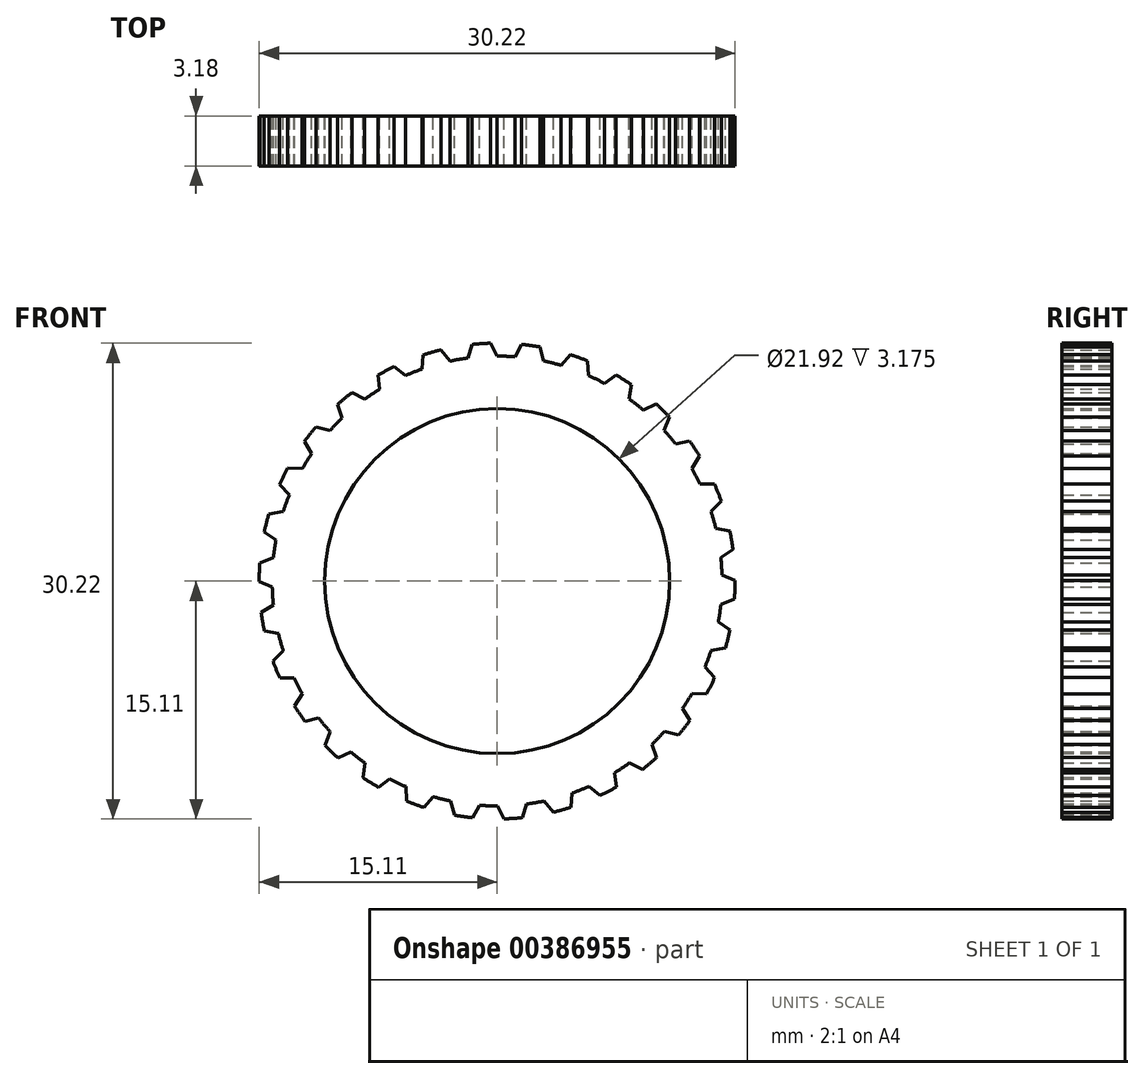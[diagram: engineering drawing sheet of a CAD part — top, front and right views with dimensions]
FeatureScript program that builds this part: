
annotation { "Feature Type Name" : "Feature", "Feature Type Description" : "" }
export const myFeature = defineFeature(function(context is Context, id is Id, definition is map)
    precondition{}
    {
        {
            var Q0;
            Q0=qCreatedBy(makeId("Front.planeOp"),FACE);
            var sketch = newSketch(context, id + "F0", { "sketchPlane" : qUnion([Q0])});
            skCircle(sketch, "E0", {"center": v(0, 0) * mm, "radius": 14.29 * mm});
            skCircle(sketch, "E1", {"center": v(0, 0) * mm, "radius": 10.96 * mm});
            skSolve(sketch);
        }
        {
            var Q0;
            Q0=qSketchRegion(id+"F0",true);
            extrude(context, id + "F1", {"entities" : qUnion([Q0]), "depth" : 3.17 * mm, "offsetDistance" : 25.4 * mm});
        }
        {
            var Q0;
            Q0=qCreatedBy(makeId("Front.planeOp"),FACE);
            var sketch = newSketch(context, id + "F2", { "sketchPlane" : qUnion([Q0])});
            skLineSegment(sketch, "E2", {"start": v(0, 0) * mm, "end": v(0, 17.22) * mm, "construction": true});
            skLineSegment(sketch, "E3", {"start": v(0, 0) * mm, "end": v(-3.55, 16.72) * mm, "construction": true});
            skLineSegment(sketch, "E4", {"start": v(0, 0) * mm, "end": v(-1.81, 17.23) * mm, "construction": true});
            skArc(sketch, "E5", {"start": v(-0.43, 15.1) * mm, "mid": v(-1.02, 15.08) * mm, "end": v(-1.6, 15.03) * mm});
            skLineSegment(sketch, "E6", {"start": v(0, 14.27) * mm, "end": v(-0.43, 15.1) * mm});
            skLineSegment(sketch, "E7", {"start": v(-1.6, 15.03) * mm, "end": v(-1.9, 14.05) * mm});
            skLineSegment(sketch, "E8", {"start": v(-1.9, 14.05) * mm, "end": v(0, 14.27) * mm});
            skLineSegment(sketch, "E9.1.0", {"start": v(-4.7, 14.37) * mm, "end": v(-4.78, 13.35) * mm});
            skArc(sketch, "E9.1.1", {"start": v(-3.56, 14.69) * mm, "mid": v(-4.13, 14.54) * mm, "end": v(-4.7, 14.37) * mm});
            skLineSegment(sketch, "E9.1.2", {"start": v(-2.97, 13.95) * mm, "end": v(-3.56, 14.69) * mm});
            skLineSegment(sketch, "E9.1.3", {"start": v(-4.78, 13.35) * mm, "end": v(-2.97, 13.95) * mm});
            skLineSegment(sketch, "E9.2.0", {"start": v(-7.58, 13.08) * mm, "end": v(-7.45, 12.06) * mm});
            skArc(sketch, "E9.2.1", {"start": v(-6.54, 13.62) * mm, "mid": v(-7.06, 13.36) * mm, "end": v(-7.58, 13.08) * mm});
            skLineSegment(sketch, "E9.2.2", {"start": v(-5.8, 13.03) * mm, "end": v(-6.54, 13.62) * mm});
            skLineSegment(sketch, "E9.2.3", {"start": v(-7.45, 12.06) * mm, "end": v(-5.8, 13.03) * mm});
            skLineSegment(sketch, "E9.3.0", {"start": v(-10.13, 11.21) * mm, "end": v(-9.8, 10.25) * mm});
            skArc(sketch, "E9.3.1", {"start": v(-9.23, 11.97) * mm, "mid": v(-9.69, 11.6) * mm, "end": v(-10.13, 11.21) * mm});
            skLineSegment(sketch, "E9.3.2", {"start": v(-8.39, 11.54) * mm, "end": v(-9.23, 11.97) * mm});
            skLineSegment(sketch, "E9.3.3", {"start": v(-9.8, 10.25) * mm, "end": v(-8.39, 11.54) * mm});
            skLineSegment(sketch, "E9.4.0", {"start": v(-12.24, 8.86) * mm, "end": v(-11.71, 8) * mm});
            skArc(sketch, "E9.4.1", {"start": v(-11.52, 9.79) * mm, "mid": v(-11.89, 9.33) * mm, "end": v(-12.24, 8.86) * mm});
            skLineSegment(sketch, "E9.4.2", {"start": v(-10.6, 9.55) * mm, "end": v(-11.52, 9.79) * mm});
            skLineSegment(sketch, "E9.4.3", {"start": v(-11.71, 8) * mm, "end": v(-10.6, 9.55) * mm});
            skLineSegment(sketch, "E9.5.0", {"start": v(-13.82, 6.12) * mm, "end": v(-13.12, 5.38) * mm});
            skArc(sketch, "E9.5.1", {"start": v(-13.3, 7.18) * mm, "mid": v(-13.57, 6.66) * mm, "end": v(-13.82, 6.12) * mm});
            skLineSegment(sketch, "E9.5.2", {"start": v(-12.35, 7.13) * mm, "end": v(-13.3, 7.18) * mm});
            skLineSegment(sketch, "E9.5.3", {"start": v(-13.12, 5.38) * mm, "end": v(-12.35, 7.13) * mm});
            skLineSegment(sketch, "E9.6.0", {"start": v(-14.79, 3.12) * mm, "end": v(-13.95, 2.54) * mm});
            skArc(sketch, "E9.6.1", {"start": v(-14.5, 4.26) * mm, "mid": v(-14.66, 3.69) * mm, "end": v(-14.79, 3.12) * mm});
            skLineSegment(sketch, "E9.6.2", {"start": v(-13.57, 4.4) * mm, "end": v(-14.5, 4.26) * mm});
            skLineSegment(sketch, "E9.6.3", {"start": v(-13.95, 2.54) * mm, "end": v(-13.57, 4.4) * mm});
            skLineSegment(sketch, "E9.7.0", {"start": v(-15.11, -0.02) * mm, "end": v(-14.17, -0.42) * mm});
            skArc(sketch, "E9.7.1", {"start": v(-15.07, 1.15) * mm, "mid": v(-15.1, 0.56) * mm, "end": v(-15.11, -0.02) * mm});
            skLineSegment(sketch, "E9.7.2", {"start": v(-14.19, 1.5) * mm, "end": v(-15.07, 1.15) * mm});
            skLineSegment(sketch, "E9.7.3", {"start": v(-14.17, -0.42) * mm, "end": v(-14.19, 1.5) * mm});
            skLineSegment(sketch, "E9.8.0", {"start": v(-14.78, -3.17) * mm, "end": v(-13.78, -3.36) * mm});
            skArc(sketch, "E9.8.1", {"start": v(-14.98, -2.01) * mm, "mid": v(-14.89, -2.6) * mm, "end": v(-14.78, -3.17) * mm});
            skLineSegment(sketch, "E9.8.2", {"start": v(-14.19, -1.5) * mm, "end": v(-14.98, -2.01) * mm});
            skLineSegment(sketch, "E9.8.3", {"start": v(-13.78, -3.36) * mm, "end": v(-14.19, -1.5) * mm});
            skLineSegment(sketch, "E9.9.0", {"start": v(-13.8, -6.17) * mm, "end": v(-12.78, -6.15) * mm});
            skArc(sketch, "E9.9.1", {"start": v(-14.23, -5.08) * mm, "mid": v(-14.03, -5.63) * mm, "end": v(-13.8, -6.17) * mm});
            skLineSegment(sketch, "E9.9.2", {"start": v(-13.57, -4.4) * mm, "end": v(-14.23, -5.08) * mm});
            skLineSegment(sketch, "E9.9.3", {"start": v(-12.78, -6.15) * mm, "end": v(-13.57, -4.4) * mm});
            skLineSegment(sketch, "E9.10.0", {"start": v(-12.21, -8.9) * mm, "end": v(-11.22, -8.67) * mm});
            skArc(sketch, "E9.10.1", {"start": v(-12.87, -7.93) * mm, "mid": v(-12.55, -8.42) * mm, "end": v(-12.21, -8.9) * mm});
            skLineSegment(sketch, "E9.10.2", {"start": v(-12.35, -7.13) * mm, "end": v(-12.87, -7.93) * mm});
            skLineSegment(sketch, "E9.10.3", {"start": v(-11.22, -8.67) * mm, "end": v(-12.35, -7.13) * mm});
            skLineSegment(sketch, "E9.11.0", {"start": v(-10.1, -11.25) * mm, "end": v(-9.17, -10.81) * mm});
            skArc(sketch, "E9.11.1", {"start": v(-10.94, -10.43) * mm, "mid": v(-10.52, -10.85) * mm, "end": v(-10.1, -11.25) * mm});
            skLineSegment(sketch, "E9.11.2", {"start": v(-10.6, -9.55) * mm, "end": v(-10.94, -10.43) * mm});
            skLineSegment(sketch, "E9.11.3", {"start": v(-9.17, -10.81) * mm, "end": v(-10.6, -9.55) * mm});
            skLineSegment(sketch, "E9.12.0", {"start": v(-7.54, -13.1) * mm, "end": v(-6.72, -12.48) * mm});
            skArc(sketch, "E9.12.1", {"start": v(-8.53, -12.48) * mm, "mid": v(-8.04, -12.8) * mm, "end": v(-7.54, -13.1) * mm});
            skLineSegment(sketch, "E9.12.2", {"start": v(-8.39, -11.54) * mm, "end": v(-8.53, -12.48) * mm});
            skLineSegment(sketch, "E9.12.3", {"start": v(-6.72, -12.48) * mm, "end": v(-8.39, -11.54) * mm});
            skLineSegment(sketch, "E9.13.0", {"start": v(-4.65, -14.38) * mm, "end": v(-3.98, -13.6) * mm});
            skArc(sketch, "E9.13.1", {"start": v(-5.75, -13.98) * mm, "mid": v(-5.2, -14.19) * mm, "end": v(-4.65, -14.38) * mm});
            skLineSegment(sketch, "E9.13.2", {"start": v(-5.8, -13.03) * mm, "end": v(-5.75, -13.98) * mm});
            skLineSegment(sketch, "E9.13.3", {"start": v(-3.98, -13.6) * mm, "end": v(-5.8, -13.03) * mm});
            skLineSegment(sketch, "E9.14.0", {"start": v(-1.56, -15.03) * mm, "end": v(-1.07, -14.14) * mm});
            skArc(sketch, "E9.14.1", {"start": v(-2.72, -14.87) * mm, "mid": v(-2.14, -14.96) * mm, "end": v(-1.56, -15.03) * mm});
            skLineSegment(sketch, "E9.14.2", {"start": v(-2.97, -13.95) * mm, "end": v(-2.72, -14.87) * mm});
            skLineSegment(sketch, "E9.14.3", {"start": v(-1.07, -14.14) * mm, "end": v(-2.97, -13.95) * mm});
            skLineSegment(sketch, "E9.15.0", {"start": v(1.6, -15.03) * mm, "end": v(1.9, -14.05) * mm});
            skArc(sketch, "E9.15.1", {"start": v(0.43, -15.1) * mm, "mid": v(1.02, -15.08) * mm, "end": v(1.6, -15.03) * mm});
            skLineSegment(sketch, "E9.15.2", {"start": v(0, -14.27) * mm, "end": v(0.43, -15.1) * mm});
            skLineSegment(sketch, "E9.15.3", {"start": v(1.9, -14.05) * mm, "end": v(0, -14.27) * mm});
            skLineSegment(sketch, "E9.16.0", {"start": v(4.7, -14.37) * mm, "end": v(4.78, -13.35) * mm});
            skArc(sketch, "E9.16.1", {"start": v(3.56, -14.69) * mm, "mid": v(4.13, -14.54) * mm, "end": v(4.7, -14.37) * mm});
            skLineSegment(sketch, "E9.16.2", {"start": v(2.97, -13.95) * mm, "end": v(3.56, -14.69) * mm});
            skLineSegment(sketch, "E9.16.3", {"start": v(4.78, -13.35) * mm, "end": v(2.97, -13.95) * mm});
            skLineSegment(sketch, "E9.17.0", {"start": v(7.58, -13.08) * mm, "end": v(7.45, -12.06) * mm});
            skArc(sketch, "E9.17.1", {"start": v(6.54, -13.62) * mm, "mid": v(7.06, -13.36) * mm, "end": v(7.58, -13.08) * mm});
            skLineSegment(sketch, "E9.17.2", {"start": v(5.8, -13.03) * mm, "end": v(6.54, -13.62) * mm});
            skLineSegment(sketch, "E9.17.3", {"start": v(7.45, -12.06) * mm, "end": v(5.8, -13.03) * mm});
            skLineSegment(sketch, "E9.18.0", {"start": v(10.13, -11.21) * mm, "end": v(9.8, -10.25) * mm});
            skArc(sketch, "E9.18.1", {"start": v(9.23, -11.97) * mm, "mid": v(9.69, -11.6) * mm, "end": v(10.13, -11.21) * mm});
            skLineSegment(sketch, "E9.18.2", {"start": v(8.39, -11.54) * mm, "end": v(9.23, -11.97) * mm});
            skLineSegment(sketch, "E9.18.3", {"start": v(9.8, -10.25) * mm, "end": v(8.39, -11.54) * mm});
            skLineSegment(sketch, "E9.19.0", {"start": v(12.24, -8.86) * mm, "end": v(11.71, -8) * mm});
            skArc(sketch, "E9.19.1", {"start": v(11.52, -9.79) * mm, "mid": v(11.89, -9.33) * mm, "end": v(12.24, -8.86) * mm});
            skLineSegment(sketch, "E9.19.2", {"start": v(10.6, -9.55) * mm, "end": v(11.52, -9.79) * mm});
            skLineSegment(sketch, "E9.19.3", {"start": v(11.71, -8) * mm, "end": v(10.6, -9.55) * mm});
            skLineSegment(sketch, "E9.20.0", {"start": v(13.82, -6.12) * mm, "end": v(13.12, -5.38) * mm});
            skArc(sketch, "E9.20.1", {"start": v(13.3, -7.18) * mm, "mid": v(13.57, -6.66) * mm, "end": v(13.82, -6.12) * mm});
            skLineSegment(sketch, "E9.20.2", {"start": v(12.35, -7.13) * mm, "end": v(13.3, -7.18) * mm});
            skLineSegment(sketch, "E9.20.3", {"start": v(13.12, -5.38) * mm, "end": v(12.35, -7.13) * mm});
            skLineSegment(sketch, "E9.21.0", {"start": v(14.79, -3.12) * mm, "end": v(13.95, -2.54) * mm});
            skArc(sketch, "E9.21.1", {"start": v(14.5, -4.26) * mm, "mid": v(14.66, -3.69) * mm, "end": v(14.79, -3.12) * mm});
            skLineSegment(sketch, "E9.21.2", {"start": v(13.57, -4.4) * mm, "end": v(14.5, -4.26) * mm});
            skLineSegment(sketch, "E9.21.3", {"start": v(13.95, -2.54) * mm, "end": v(13.57, -4.4) * mm});
            skLineSegment(sketch, "E9.22.0", {"start": v(15.11, 0.02) * mm, "end": v(14.17, 0.42) * mm});
            skArc(sketch, "E9.22.1", {"start": v(15.07, -1.15) * mm, "mid": v(15.1, -0.56) * mm, "end": v(15.11, 0.02) * mm});
            skLineSegment(sketch, "E9.22.2", {"start": v(14.19, -1.5) * mm, "end": v(15.07, -1.15) * mm});
            skLineSegment(sketch, "E9.22.3", {"start": v(14.17, 0.42) * mm, "end": v(14.19, -1.5) * mm});
            skLineSegment(sketch, "E9.23.0", {"start": v(14.78, 3.17) * mm, "end": v(13.78, 3.36) * mm});
            skArc(sketch, "E9.23.1", {"start": v(14.98, 2.01) * mm, "mid": v(14.89, 2.6) * mm, "end": v(14.78, 3.17) * mm});
            skLineSegment(sketch, "E9.23.2", {"start": v(14.19, 1.5) * mm, "end": v(14.98, 2.01) * mm});
            skLineSegment(sketch, "E9.23.3", {"start": v(13.78, 3.36) * mm, "end": v(14.19, 1.5) * mm});
            skLineSegment(sketch, "E9.24.0", {"start": v(13.8, 6.17) * mm, "end": v(12.78, 6.15) * mm});
            skArc(sketch, "E9.24.1", {"start": v(14.23, 5.08) * mm, "mid": v(14.03, 5.63) * mm, "end": v(13.8, 6.17) * mm});
            skLineSegment(sketch, "E9.24.2", {"start": v(13.57, 4.4) * mm, "end": v(14.23, 5.08) * mm});
            skLineSegment(sketch, "E9.24.3", {"start": v(12.78, 6.15) * mm, "end": v(13.57, 4.4) * mm});
            skLineSegment(sketch, "E9.25.0", {"start": v(12.21, 8.9) * mm, "end": v(11.22, 8.67) * mm});
            skArc(sketch, "E9.25.1", {"start": v(12.87, 7.93) * mm, "mid": v(12.55, 8.42) * mm, "end": v(12.21, 8.9) * mm});
            skLineSegment(sketch, "E9.25.2", {"start": v(12.35, 7.13) * mm, "end": v(12.87, 7.93) * mm});
            skLineSegment(sketch, "E9.25.3", {"start": v(11.22, 8.67) * mm, "end": v(12.35, 7.13) * mm});
            skLineSegment(sketch, "E9.26.0", {"start": v(10.1, 11.25) * mm, "end": v(9.17, 10.81) * mm});
            skArc(sketch, "E9.26.1", {"start": v(10.94, 10.43) * mm, "mid": v(10.52, 10.85) * mm, "end": v(10.1, 11.25) * mm});
            skLineSegment(sketch, "E9.26.2", {"start": v(10.6, 9.55) * mm, "end": v(10.94, 10.43) * mm});
            skLineSegment(sketch, "E9.26.3", {"start": v(9.17, 10.81) * mm, "end": v(10.6, 9.55) * mm});
            skLineSegment(sketch, "E9.27.0", {"start": v(7.54, 13.1) * mm, "end": v(6.72, 12.48) * mm});
            skArc(sketch, "E9.27.1", {"start": v(8.53, 12.48) * mm, "mid": v(8.04, 12.8) * mm, "end": v(7.54, 13.1) * mm});
            skLineSegment(sketch, "E9.27.2", {"start": v(8.39, 11.54) * mm, "end": v(8.53, 12.48) * mm});
            skLineSegment(sketch, "E9.27.3", {"start": v(6.72, 12.48) * mm, "end": v(8.39, 11.54) * mm});
            skLineSegment(sketch, "E9.28.0", {"start": v(4.65, 14.38) * mm, "end": v(3.98, 13.6) * mm});
            skArc(sketch, "E9.28.1", {"start": v(5.75, 13.98) * mm, "mid": v(5.2, 14.19) * mm, "end": v(4.65, 14.38) * mm});
            skLineSegment(sketch, "E9.28.2", {"start": v(5.8, 13.03) * mm, "end": v(5.75, 13.98) * mm});
            skLineSegment(sketch, "E9.28.3", {"start": v(3.98, 13.6) * mm, "end": v(5.8, 13.03) * mm});
            skLineSegment(sketch, "E9.29.0", {"start": v(1.56, 15.03) * mm, "end": v(1.07, 14.14) * mm});
            skArc(sketch, "E9.29.1", {"start": v(2.72, 14.87) * mm, "mid": v(2.14, 14.96) * mm, "end": v(1.56, 15.03) * mm});
            skLineSegment(sketch, "E9.29.2", {"start": v(2.97, 13.95) * mm, "end": v(2.72, 14.87) * mm});
            skLineSegment(sketch, "E9.29.3", {"start": v(1.07, 14.14) * mm, "end": v(2.97, 13.95) * mm});
            skSolve(sketch);
        }
        {
            var Q0;
            Q0=qSketchRegion(id+"F2",true);
            var Q1;
            {var subQ0=sQuery(id+"F0.wireOp",EDGE,"E0");Q1=makeQuery(id+"FgRAGb1TDaWAYW9_1.boolean.opBoolean","SPLIT",FACE,{"disambiguationData":[TD([makeQuery(id+"F1.opExtrude","SWEPT_FACE",FACE,{"disambiguationData":[OSD([subQ0])]})])],"derivedFrom":makeQuery(id+"F1.opExtrude","CAP_FACE",FACE,{"disambiguationData":[OSD([subQ0,sQuery(id+"F0.wireOp",EDGE,"E1")])],"isStart":false})});}
            extrude(context, id + "F3", {"entities" : qUnion([Q0]), "operationType" : NewBodyOperationType.ADD, "endBound" : BoundingType.UP_TO_SURFACE, "endBoundEntityFace" : qUnion([Q1]), "depth" : 25.4 * mm, "offsetDistance" : 25.4 * mm});
        }
    });
